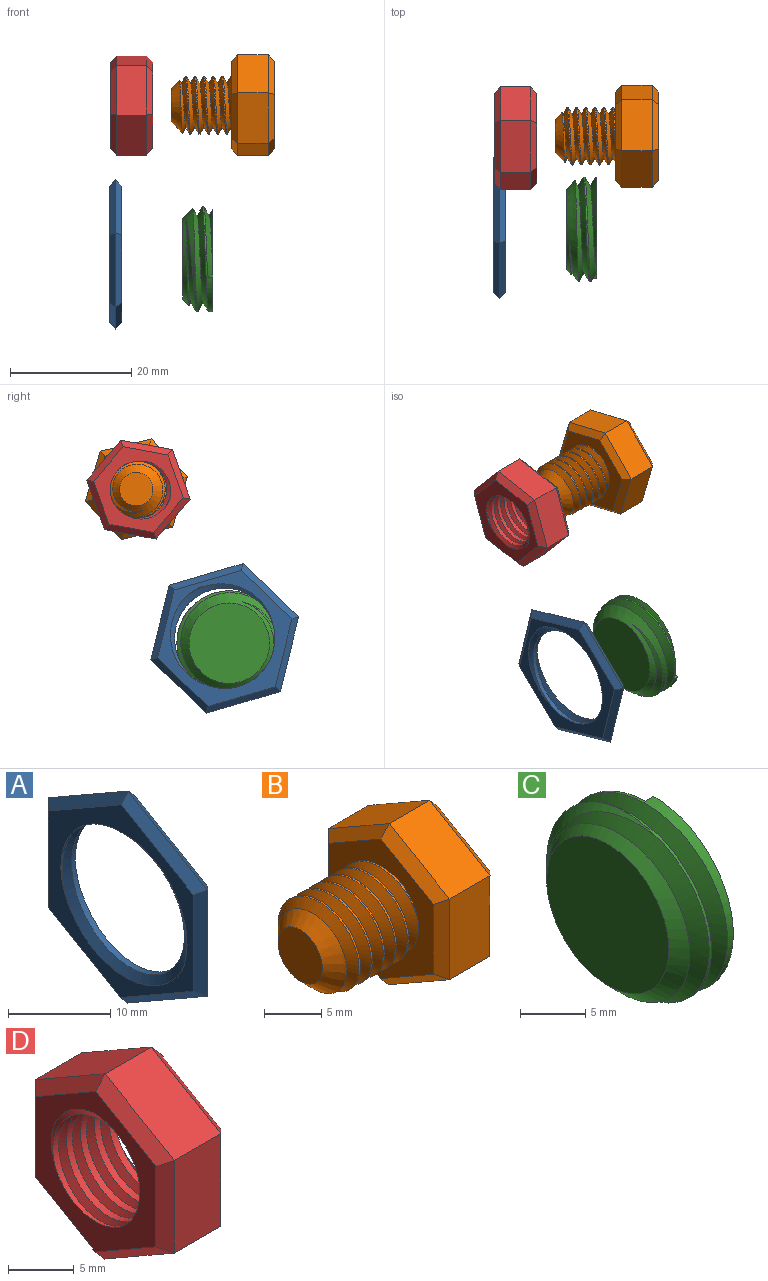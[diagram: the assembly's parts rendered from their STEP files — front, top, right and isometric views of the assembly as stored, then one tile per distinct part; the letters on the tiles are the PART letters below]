
ASSEMBLY  parts=4 mates=2
PART A: 17 faces, bbox 4.3x22.7x26.1 mm
  f0: cylinder r=8.28mm len=16.56mm, axis (1,0,0), area 36.6mm2, adj f1,f2,f15,f16
  f1: plane 23.74x20.68mm, normal (-1,0,0), area 111.3mm2, adj f0,f3,f4,f5,f6,f7,f8,f15
  f2: plane 23.74x20.68mm, normal (1,0,0), area 111.3mm2, adj f0,f9,f10,f11,f12,f13,f14,f15
  f3: plane 10.99x6.96mm, normal (-0.71,0.36,-0.61), area 17.1mm2, adj f1,f4,f5,f11
  f4: plane 11.02x6.9mm, normal (-0.71,-0.35,-0.61), area 17.1mm2, adj f1,f3,f6,f9
  f5: plane 12.7x1.03mm, normal (-0.71,0.71,0), area 17.1mm2, adj f1,f3,f7,f13
  f6: plane 12.7x1.03mm, normal (-0.71,-0.71,0), area 17.1mm2, adj f1,f4,f8,f10
  f7: plane 11.02x6.9mm, normal (-0.71,0.35,0.61), area 17.1mm2, adj f1,f5,f8,f14
  f8: plane 10.99x6.96mm, normal (-0.71,-0.36,0.61), area 17.1mm2, adj f1,f6,f7,f12
  f9: plane 11.02x6.9mm, normal (0.71,-0.35,-0.61), area 17.1mm2, adj f2,f4,f10,f11
  f10: plane 12.7x1.03mm, normal (0.71,-0.71,0), area 17.1mm2, adj f2,f6,f9,f12
  f11: plane 10.99x6.96mm, normal (0.71,0.36,-0.61), area 17.1mm2, adj f2,f3,f9,f13
  f12: plane 10.99x6.96mm, normal (0.71,-0.36,0.61), area 17.1mm2, adj f2,f8,f10,f14
  f13: plane 12.7x1.03mm, normal (0.71,0.71,0), area 17.1mm2, adj f2,f5,f11,f14
  f14: plane 11.02x6.9mm, normal (0.71,0.35,0.61), area 17.1mm2, adj f2,f7,f12,f13
  f15: bspline ~21.71x18.81mm, area 72.2mm2, adj f0,f1,f2,f16
  f16: bspline ~21.71x18.81mm, area 72.2mm2, adj f0,f1,f2,f15
PART B: 25 faces, bbox 17.8x15.9x18.1 mm
  f0: cylinder r=4.75mm len=9.5mm, axis (1,0,0), area 28.1mm2, adj f1,f2,f4,f12
  f1: bspline ~10.97x9.91mm, area 196.7mm2, adj f0,f2,f4,f12
  f2: bspline ~10.97x10.66mm, area 196.6mm2, adj f0,f1,f4,f12
  f3: plane 5.5x5.5mm, normal (-1,0,0), area 23.8mm2, adj f4
  f4: cone r=4.75mm half-angle=45deg, axis (1,0,0), area 47.4mm2, adj f0,f1,f2,f3
  f5: plane 7.48x5mm, normal (0,-0.5,0.86), area 43.3mm2, adj f6,f10,f18,f22
  f6: plane 8.66x5mm, normal (0,-1,0), area 43.3mm2, adj f5,f7,f16,f20
  f7: plane 7.52x5mm, normal (0,-0.5,-0.87), area 43.3mm2, adj f6,f8,f14,f19
  f8: plane 7.48x5mm, normal (0,0.5,-0.86), area 43.3mm2, adj f7,f9,f13,f21
  f9: plane 8.66x5mm, normal (0,1,0), area 43.3mm2, adj f8,f10,f15,f23
  f10: plane 7.52x5mm, normal (0,0.5,0.87), area 43.3mm2, adj f5,f9,f17,f24
  f11: plane 15.01x13.03mm, normal (1,0,0), area 146.4mm2, adj f13,f14,f15,f16,f17,f18
  f12: plane 15.83x13.85mm, normal (-1,0,0), area 89.2mm2, adj f0,f1,f2,f19,f20,f21,f22,f23
  f13: plane 7.49x4.93mm, normal (0.71,0.36,-0.61), area 11.4mm2, adj f8,f11,f14,f15
  f14: plane 7.52x4.88mm, normal (0.71,-0.35,-0.61), area 11.4mm2, adj f7,f11,f13,f16
  f15: plane 8.66x1.03mm, normal (0.71,0.71,0), area 11.4mm2, adj f9,f11,f13,f17
  f16: plane 8.66x1.03mm, normal (0.71,-0.71,0), area 11.4mm2, adj f6,f11,f14,f18
  f17: plane 7.52x4.88mm, normal (0.71,0.35,0.61), area 11.4mm2, adj f10,f11,f15,f18
  f18: plane 7.49x4.93mm, normal (0.71,-0.36,0.61), area 11.4mm2, adj f5,f11,f16,f17
  f19: plane 7.52x4.88mm, normal (-0.71,-0.35,-0.61), area 11.4mm2, adj f7,f12,f20,f21
  f20: plane 8.66x1.03mm, normal (-0.71,-0.71,0), area 11.4mm2, adj f6,f12,f19,f22
  f21: plane 7.49x4.93mm, normal (-0.71,0.36,-0.61), area 11.4mm2, adj f8,f12,f19,f23
  f22: plane 7.49x4.93mm, normal (-0.71,-0.36,0.61), area 11.4mm2, adj f5,f12,f20,f24
  f23: plane 8.66x1.03mm, normal (-0.71,0.71,0), area 11.4mm2, adj f9,f12,f21,f24
  f24: plane 7.52x4.88mm, normal (-0.71,0.35,0.61), area 11.4mm2, adj f10,f12,f22,f23
PART C: 7 faces, bbox 7.5x21.1x18.4 mm
  f0: cylinder r=8.64mm len=17.28mm, axis (1,0,0), area 30.8mm2, adj f2,f3,f4,f5,f6
  f1: plane 13.28x13.28mm, normal (-1,0,0), area 138.5mm2, adj f3
  f2: plane 18.4x17.78mm, normal (1,0,0), area 217.6mm2, adj f0,f4,f5
  f3: cone r=8.64mm half-angle=45deg, axis (1,0,0), area 87.9mm2, adj f0,f1,f5,f6
  f4: plane 1.52x0.88mm, normal (0,1,0), area 0.7mm2, adj f0,f2,f6
  f5: bspline ~19.95x17.28mm, area 162mm2, adj f0,f2,f3,f6
  f6: bspline ~19.95x17.28mm, area 142.3mm2, adj f0,f3,f4,f5
PART D: 23 faces, bbox 9.1x15.4x17.7 mm
  f0: plane 7.49x5mm, normal (0,-0.5,0.86), area 43.3mm2, adj f1,f5,f13,f17
  f1: plane 8.66x5mm, normal (0,-1,0), area 43.3mm2, adj f0,f2,f11,f15
  f2: plane 7.51x5mm, normal (0,-0.5,-0.87), area 43.3mm2, adj f1,f3,f9,f14
  f3: plane 7.49x5mm, normal (0,0.5,-0.86), area 43.3mm2, adj f2,f4,f8,f16
  f4: plane 8.66x5mm, normal (0,1,0), area 43.3mm2, adj f3,f5,f10,f18
  f5: plane 7.51x5mm, normal (0,0.5,0.87), area 43.3mm2, adj f0,f4,f12,f19
  f6: plane 15.37x13.38mm, normal (-1,0,0), area 71.4mm2, adj f8,f9,f10,f11,f12,f13,f20,f21
  f7: plane 15.37x13.38mm, normal (1,0,0), area 71.4mm2, adj f14,f15,f16,f17,f18,f19,f20,f21
  f8: plane 7.49x4.93mm, normal (-0.71,0.36,-0.61), area 11.4mm2, adj f3,f6,f9,f10
  f9: plane 7.51x4.89mm, normal (-0.71,-0.35,-0.61), area 11.4mm2, adj f2,f6,f8,f11
  f10: plane 8.66x1.02mm, normal (-0.71,0.71,0), area 11.4mm2, adj f4,f6,f8,f12
  f11: plane 8.66x1.02mm, normal (-0.71,-0.71,0), area 11.4mm2, adj f1,f6,f9,f13
  f12: plane 7.51x4.89mm, normal (-0.71,0.35,0.61), area 11.4mm2, adj f5,f6,f10,f13
  f13: plane 7.49x4.93mm, normal (-0.71,-0.36,0.61), area 11.4mm2, adj f0,f6,f11,f12
  f14: plane 7.51x4.89mm, normal (0.71,-0.35,-0.61), area 11.4mm2, adj f2,f7,f15,f16
  f15: plane 8.66x1.02mm, normal (0.71,-0.71,0), area 11.4mm2, adj f1,f7,f14,f17
  f16: plane 7.49x4.93mm, normal (0.71,0.36,-0.61), area 11.4mm2, adj f3,f7,f14,f18
  f17: plane 7.49x4.93mm, normal (0.71,-0.36,0.61), area 11.4mm2, adj f0,f7,f15,f19
  f18: plane 8.66x1.02mm, normal (0.71,0.71,0), area 11.4mm2, adj f4,f7,f16,f19
  f19: plane 7.51x4.89mm, normal (0.71,0.35,0.61), area 11.4mm2, adj f5,f7,f17,f18
  f20: cylinder r=4.66mm len=9.32mm, axis (1,0,0), area 85.4mm2, adj f6,f7,f21,f22
  f21: bspline ~12.5x10.82mm, area 128.4mm2, adj f6,f7,f20,f22
  f22: bspline ~12.5x10.82mm, area 128.5mm2, adj f6,f7,f20,f21
PLACE A rot(axis=(0,0.6,-0.8),180deg) t=(-55.27,-6.86,23.48)mm fixed
PLACE B rot(axis=(-1,0,0),43.8deg) t=(-31.66,7.73,48.08)mm
PLACE C rot(axis=(1,0,0),109.9deg) t=(-38.27,-7.6,22.68)mm
PLACE D rot(axis=(1,0,0),100.2deg) t=(-48.16,7.38,48.02)mm fixed
MATE cylindrical C.f0 <-> A.f1  axis (-1,0,0) through (-43.27,-7.6,22.68)mm
MATE cylindrical B.f0 <-> D.f6  axis (-1,0,0) through (-45.16,7.73,48.08)mm
